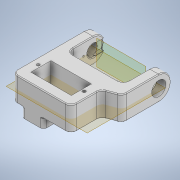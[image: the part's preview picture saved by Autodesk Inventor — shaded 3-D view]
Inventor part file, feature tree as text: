
AUTODESK INVENTOR PART (.ipt)
format: ipt  version: 2020.3 (Build 243373000, 373)  size: 463,360 bytes
history: native  units: mm
features: sketch x8, other x3, plane x3
ambient origin geometry x8: Origin, YZ Plane, XZ Plane, XY Plane, X Axis, Y Axis, Z Axis, Center Point
bodies: Solid1 (feature_tree)
feature tree (14):
  other  "LegStart_v1.ipt"
  plane  "Work Plane4"
  plane  "Work Plane5"
  other  "Solid1::LegStart_v1.ipt"
  other  "TaggingFeature1"
  sketch  "Sketch1"  dims[d0=10.0mm]
  sketch  "Sketch2"  dims[d1=16.0mm]
  sketch  "Sketch3"  dims[d2=-7.5mm]
  sketch  "Sketch8"
  sketch  "Sketch9"
  sketch  "Sketch10"
  sketch  "Sketch11"
  sketch  "Sketch12"
  plane  "Work Plane1"
